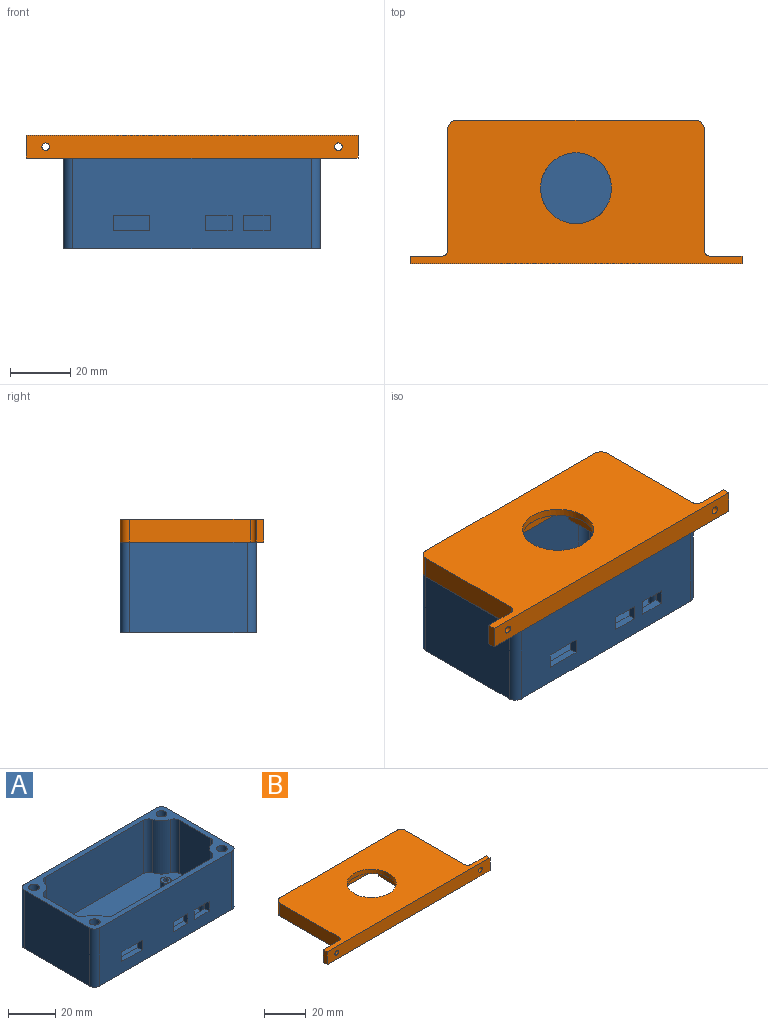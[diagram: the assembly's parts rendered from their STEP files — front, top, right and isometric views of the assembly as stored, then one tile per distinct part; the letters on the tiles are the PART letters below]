
ASSEMBLY  parts=2 mates=1
PART A: 59 faces, bbox 85x45x30 mm
  f0: plane 58.83x27.5mm, normal (0,-1,0), area 1617.9mm2, adj f1,f6,f44,f49
  f1: plane 80x40mm, normal (0,0,1), area 2925.6mm2, adj f0,f2,f3,f4,f12,f16,f20,f24
  f2: plane 58.83x27.5mm, normal (0,1,0), area 1470.4mm2, adj f1,f6,f27,f28,f29,f30,f31,f32
  f3: plane 27.5x18.83mm, normal (-1,0,0), area 517.9mm2, adj f1,f6,f43,f45
  f4: plane 27.5x18.83mm, normal (1,0,0), area 517.9mm2, adj f1,f6,f47,f50
  f5: plane 79x30mm, normal (0,-1,0), area 2222.5mm2, adj f6,f10,f27,f28,f29,f30,f31,f32
  f6: plane 85x45mm, normal (0,0,1), area 764.4mm2, adj f0,f2,f3,f4,f5,f7,f8,f9
  f7: plane 79x30mm, normal (0,1,0), area 2370mm2, adj f6,f10,f51,f54
  f8: plane 39x30mm, normal (-1,0,0), area 1170mm2, adj f6,f10,f51,f52
  f9: plane 39x30mm, normal (1,0,0), area 1170mm2, adj f6,f10,f53,f54
  f10: plane 85x45mm, normal (0,0,-1), area 3753.7mm2, adj f5,f7,f8,f9,f51,f52,f53,f54
  f11: cylinder r=1.03mm len=3.5mm, axis (0,0,1), area 22.5mm2, adj f13,f14
  f12: cylinder r=2.25mm len=4.5mm, axis (0,0,1), area 49.5mm2, adj f1,f13
  f13: plane 4.5x4.5mm, normal (0,0,1), area 12.6mm2, adj f11,f12
  f14: plane 2.05x2.05mm, normal (0,0,1), area 3.3mm2, adj f11
  f15: cylinder r=1.03mm len=3.5mm, axis (0,0,1), area 22.5mm2, adj f17,f18
  f16: cylinder r=2.25mm len=4.5mm, axis (0,0,1), area 49.5mm2, adj f1,f17
  f17: plane 4.5x4.5mm, normal (0,0,1), area 12.6mm2, adj f15,f16
  f18: plane 2.05x2.05mm, normal (0,0,1), area 3.3mm2, adj f15
  f19: cylinder r=1.03mm len=3.5mm, axis (0,0,1), area 22.5mm2, adj f21,f22
  f20: cylinder r=2.25mm len=4.5mm, axis (0,0,1), area 49.5mm2, adj f1,f21
  f21: plane 4.5x4.5mm, normal (0,0,1), area 12.6mm2, adj f19,f20
  f22: plane 2.05x2.05mm, normal (0,0,1), area 3.3mm2, adj f19
  f23: cylinder r=1.03mm len=3.5mm, axis (0,0,1), area 22.5mm2, adj f25,f26
  f24: cylinder r=2.25mm len=4.5mm, axis (0,0,1), area 49.5mm2, adj f1,f25
  f25: plane 4.5x4.5mm, normal (0,0,1), area 12.6mm2, adj f23,f24
  f26: plane 2.05x2.05mm, normal (0,0,1), area 3.3mm2, adj f23
  f27: plane 8.75x2.5mm, normal (0,0,-1), area 21.9mm2, adj f2,f5,f28,f30
  f28: plane 5x2.5mm, normal (1,0,0), area 12.5mm2, adj f2,f5,f27,f29
  f29: plane 8.75x2.5mm, normal (0,0,1), area 21.9mm2, adj f2,f5,f28,f30
  f30: plane 5x2.5mm, normal (-1,0,0), area 12.5mm2, adj f2,f5,f27,f29
  f31: plane 8.75x2.5mm, normal (0,0,-1), area 21.9mm2, adj f2,f5,f32,f34
  f32: plane 5x2.5mm, normal (1,0,0), area 12.5mm2, adj f2,f5,f31,f33
  f33: plane 8.75x2.5mm, normal (0,0,1), area 21.9mm2, adj f2,f5,f32,f34
  f34: plane 5x2.5mm, normal (-1,0,0), area 12.5mm2, adj f2,f5,f31,f33
  f35: plane 12x2.5mm, normal (0,0,-1), area 30mm2, adj f2,f5,f36,f38
  f36: plane 5x2.5mm, normal (1,0,0), area 12.5mm2, adj f2,f5,f35,f37
  f37: plane 12x2.5mm, normal (0,0,1), area 30mm2, adj f2,f5,f36,f38
  f38: plane 5x2.5mm, normal (-1,0,0), area 12.5mm2, adj f2,f5,f35,f37
  f39: cylinder r=8mm len=27.5mm, axis (0,0,-1), area 224mm2, adj f1,f6,f49,f50
  f40: cylinder r=8mm len=27.5mm, axis (0,0,-1), area 224mm2, adj f1,f6,f47,f48
  f41: cylinder r=8mm len=27.5mm, axis (0,0,-1), area 224mm2, adj f1,f6,f45,f46
  f42: cylinder r=8mm len=27.5mm, axis (0,0,-1), area 224mm2, adj f1,f6,f43,f44
  f43: cylinder r=3mm len=27.5mm, axis (0,0,-1), area 106.8mm2, adj f1,f3,f6,f42
  f44: cylinder r=3mm len=27.5mm, axis (0,0,-1), area 106.8mm2, adj f0,f1,f6,f42
  f45: cylinder r=3mm len=27.5mm, axis (0,0,-1), area 106.8mm2, adj f1,f3,f6,f41
  f46: cylinder r=3mm len=27.5mm, axis (0,0,-1), area 106.8mm2, adj f1,f2,f6,f41
  f47: cylinder r=3mm len=27.5mm, axis (0,0,-1), area 106.8mm2, adj f1,f4,f6,f40
  f48: cylinder r=3mm len=27.5mm, axis (0,0,-1), area 106.8mm2, adj f1,f2,f6,f40
  f49: cylinder r=3mm len=27.5mm, axis (0,0,-1), area 106.8mm2, adj f0,f1,f6,f39
  f50: cylinder r=3mm len=27.5mm, axis (0,0,-1), area 106.8mm2, adj f1,f4,f6,f39
  f51: cylinder r=3mm len=30mm, axis (0,0,1), area 141.4mm2, adj f6,f7,f8,f10
  f52: cylinder r=3mm len=30mm, axis (0,0,-1), area 141.4mm2, adj f5,f6,f8,f10
  f53: cylinder r=3mm len=30mm, axis (0,0,1), area 141.4mm2, adj f5,f6,f9,f10
  f54: cylinder r=3mm len=30mm, axis (0,0,-1), area 141.4mm2, adj f6,f7,f9,f10
  f55: cylinder r=2.25mm len=30mm, axis (0,0,1), area 424.1mm2, adj f6,f10
  f56: cylinder r=2.25mm len=30mm, axis (0,0,1), area 424.1mm2, adj f6,f10
  f57: cylinder r=2.25mm len=30mm, axis (0,0,1), area 424.1mm2, adj f6,f10
  f58: cylinder r=2.25mm len=30mm, axis (0,0,1), area 424.1mm2, adj f6,f10
PART B: 62 faces, bbox 110x47.5x7.5 mm
  f0: plane 13.5x2.5mm, normal (1,0,0), area 33.7mm2, adj f2,f9,f10,f20,f23
  f1: plane 13.5x2.5mm, normal (-1,0,0), area 33.7mm2, adj f2,f8,f11,f16,f19
  f2: plane 80x40mm, normal (0,0,-1), area 2330.7mm2, adj f0,f1,f12,f13,f14,f16,f17,f18
  f3: plane 79x7.5mm, normal (0,1,0), area 592.5mm2, adj f6,f34,f51,f52
  f4: plane 40x7.5mm, normal (-1,0,0), area 300mm2, adj f6,f34,f51,f58
  f5: plane 40x7.5mm, normal (1,0,0), area 300mm2, adj f6,f34,f52,f59
  f6: plane 110x47.5mm, normal (0,0,1), area 3664.1mm2, adj f3,f4,f5,f7,f51,f52,f53,f54
  f7: cylinder r=11.75mm len=23.5mm, axis (0,0,1), area 184.6mm2, adj f6,f8,f9,f10,f11
  f8: plane 16.75x11.75mm, normal (0,0,-1), area 54.6mm2, adj f1,f7,f12,f18,f19
  f9: plane 16.75x11.75mm, normal (0,0,-1), area 54.6mm2, adj f0,f7,f12,f20,f21
  f10: plane 16.75x11.75mm, normal (0,0,-1), area 54.6mm2, adj f0,f7,f13,f22,f23
  f11: plane 16.75x11.75mm, normal (0,0,-1), area 54.6mm2, adj f1,f7,f13,f16,f17
  f12: plane 33.5x2.5mm, normal (0,-1,0), area 83.8mm2, adj f2,f8,f9,f18,f21
  f13: plane 33.5x2.5mm, normal (0,1,0), area 83.8mm2, adj f2,f10,f11,f17,f22
  f14: cylinder r=1mm len=2.5mm, axis (0,0,-1), area 15.7mm2, adj f2,f15
  f15: plane 2x2mm, normal (0,0,-1), area 3.1mm2, adj f14
  f16: plane 5x2.5mm, normal (0,-1,0), area 12.5mm2, adj f1,f2,f11,f17
  f17: plane 5x2.5mm, normal (-1,0,0), area 12.5mm2, adj f2,f11,f13,f16
  f18: plane 5x2.5mm, normal (-1,0,0), area 12.5mm2, adj f2,f8,f12,f19
  f19: plane 5x2.5mm, normal (0,1,0), area 12.5mm2, adj f1,f2,f8,f18
  f20: plane 5x2.5mm, normal (0,1,0), area 12.5mm2, adj f0,f2,f9,f21
  f21: plane 5x2.5mm, normal (1,0,0), area 12.5mm2, adj f2,f9,f12,f20
  f22: plane 5x2.5mm, normal (1,0,0), area 12.5mm2, adj f2,f10,f13,f23
  f23: plane 5x2.5mm, normal (0,-1,0), area 12.5mm2, adj f0,f2,f10,f22
  f24: cylinder r=1mm len=2.5mm, axis (0,0,-1), area 15.7mm2, adj f2,f25
  f25: plane 2x2mm, normal (0,0,-1), area 3.1mm2, adj f24
  f26: cylinder r=8mm len=5.52mm, axis (0,0,1), area 20.4mm2, adj f2,f34,f43,f50
  f27: plane 18.83x2.5mm, normal (1,0,0), area 47.1mm2, adj f2,f34,f43,f44
  f28: cylinder r=8mm len=5.52mm, axis (0,0,1), area 20.4mm2, adj f2,f34,f44,f45
  f29: plane 58.83x2.5mm, normal (0,1,0), area 147.1mm2, adj f2,f34,f45,f46
  f30: cylinder r=8mm len=5.52mm, axis (0,0,1), area 20.4mm2, adj f2,f34,f46,f47
  f31: plane 18.83x2.5mm, normal (-1,0,0), area 47.1mm2, adj f2,f34,f47,f48
  f32: cylinder r=8mm len=5.52mm, axis (0,0,1), area 20.4mm2, adj f2,f34,f48,f49
  f33: plane 58.83x2.5mm, normal (0,-1,0), area 147.1mm2, adj f2,f34,f49,f50
  f34: plane 110x47.5mm, normal (0,0,-1), area 1063.2mm2, adj f3,f4,f5,f26,f27,f28,f29,f30
  f35: cylinder r=1.9mm len=5mm, axis (0,0,-1), area 59.7mm2, adj f34,f36
  f36: plane 3.8x3.8mm, normal (0,0,-1), area 11.3mm2, adj f35
  f37: cylinder r=1.9mm len=5mm, axis (0,0,-1), area 59.7mm2, adj f34,f38
  f38: plane 3.8x3.8mm, normal (0,0,-1), area 11.3mm2, adj f37
  f39: cylinder r=1.9mm len=5mm, axis (0,0,-1), area 59.7mm2, adj f34,f40
  f40: plane 3.8x3.8mm, normal (0,0,-1), area 11.3mm2, adj f39
  f41: cylinder r=1.9mm len=5mm, axis (0,0,-1), area 59.7mm2, adj f34,f42
  f42: plane 3.8x3.8mm, normal (0,0,-1), area 11.3mm2, adj f41
  f43: cylinder r=3mm len=2.89mm, axis (0,0,1), area 9.7mm2, adj f2,f26,f27,f34
  f44: cylinder r=3mm len=2.89mm, axis (0,0,1), area 9.7mm2, adj f2,f27,f28,f34
  f45: cylinder r=3mm len=2.89mm, axis (0,0,1), area 9.7mm2, adj f2,f28,f29,f34
  f46: cylinder r=3mm len=2.89mm, axis (0,0,1), area 9.7mm2, adj f2,f29,f30,f34
  f47: cylinder r=3mm len=2.89mm, axis (0,0,1), area 9.7mm2, adj f2,f30,f31,f34
  f48: cylinder r=3mm len=2.89mm, axis (0,0,1), area 9.7mm2, adj f2,f31,f32,f34
  f49: cylinder r=3mm len=2.89mm, axis (0,0,1), area 9.7mm2, adj f2,f32,f33,f34
  f50: cylinder r=3mm len=2.89mm, axis (0,0,1), area 9.7mm2, adj f2,f26,f33,f34
  f51: cylinder r=3mm len=7.5mm, axis (0,0,1), area 35.3mm2, adj f3,f4,f6,f34
  f52: cylinder r=3mm len=7.5mm, axis (0,0,-1), area 35.3mm2, adj f3,f5,f6,f34
  f53: plane 10.5x7.5mm, normal (0,1,0), area 73.8mm2, adj f6,f34,f54,f58,f61
  f54: plane 7.5x2.5mm, normal (-1,0,0), area 18.8mm2, adj f6,f34,f53,f56
  f55: plane 7.5x2.5mm, normal (1,0,0), area 18.8mm2, adj f6,f34,f56,f57
  f56: plane 110x7.5mm, normal (0,-1,0), area 815.2mm2, adj f6,f34,f54,f55,f60,f61
  f57: plane 10.5x7.5mm, normal (0,1,0), area 73.8mm2, adj f6,f34,f55,f59,f60
  f58: cylinder r=2mm len=7.5mm, axis (0,0,1), area 23.6mm2, adj f4,f6,f34,f53
  f59: cylinder r=2mm len=7.5mm, axis (0,0,-1), area 23.6mm2, adj f5,f6,f34,f57
  f60: cylinder r=1.25mm len=2.5mm, axis (0,-1,0), area 19.6mm2, adj f56,f57
  f61: cylinder r=1.25mm len=2.5mm, axis (0,-1,0), area 19.6mm2, adj f53,f56
PLACE A t=(3.9,-0.21,-36.36)mm
PLACE B t=(3.9,4.79,-3.86)mm
MATE fastened A.f6 <-> B.f34  axis (0,0,1) through (41.72,17.09,-8.86)mm
